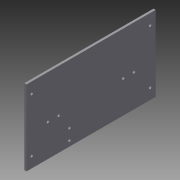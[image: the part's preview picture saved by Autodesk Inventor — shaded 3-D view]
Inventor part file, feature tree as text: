
AUTODESK INVENTOR PART (.ipt)
format: ipt  version: 2015 (Build 190159000, 159)  size: 116,736 bytes
history: native  units: in
note: dims shown in document units (in); Inventor stores cm internally (conversion verified against a paired STEP export)
features: sketch x4, extrude x2, hole x2, projected_geometry x2
ambient origin geometry x8: Origin, YZ Plane, XZ Plane, XY Plane, X Axis, Y Axis, Z Axis, Center Point
bodies: Solid1 (feature_tree)
feature tree (10):
  extrude  "Extrusion1"  Depth=6.0in
  hole  "Hole1"  [1 undecoded]
  hole  "Hole2"  [1 undecoded]
  extrude  "Extrusion2"  Depth=0.5in
  sketch  "Sketch1"  dims[d0=3.5in d1=6.0in]
  sketch  "Sketch2"  dims[d2=0.1in d3=0.0in d4=0.25in]
  projected_geometry  "Projected Loop1"
  sketch  "Sketch3"  dims[d5=0.5in d6=0.5in]
  projected_geometry  "Projected Loop2"
  sketch  "Sketch4"  dims[d7=0.5in d8=0.5in d9=0.125in d10=0.75in d11=0.375in d12=0.25in d13=0.5635in d14=1.0in d15=0.8108in d16=1.5in d17=1.0in d18=0.5in d19=0.5in d20=1.0in d21=0.125in d22=0.75in d23=0.375in d24=0.25in d25=0.5635in d26=1.0in d27=0.8108in d28=3.0in d29=1.5in d30=0.25in d31=1.0in d32=0.15in d33=0.5in d34=0.5in d35=0.125in d36=0.125in d37=1.0in d38=0.0in]
note: 2 required parameter values undecoded (feature->parameter linkage not recoverable at this tier; creation-order binding heuristic only, values carry confidence <= 0.55)
